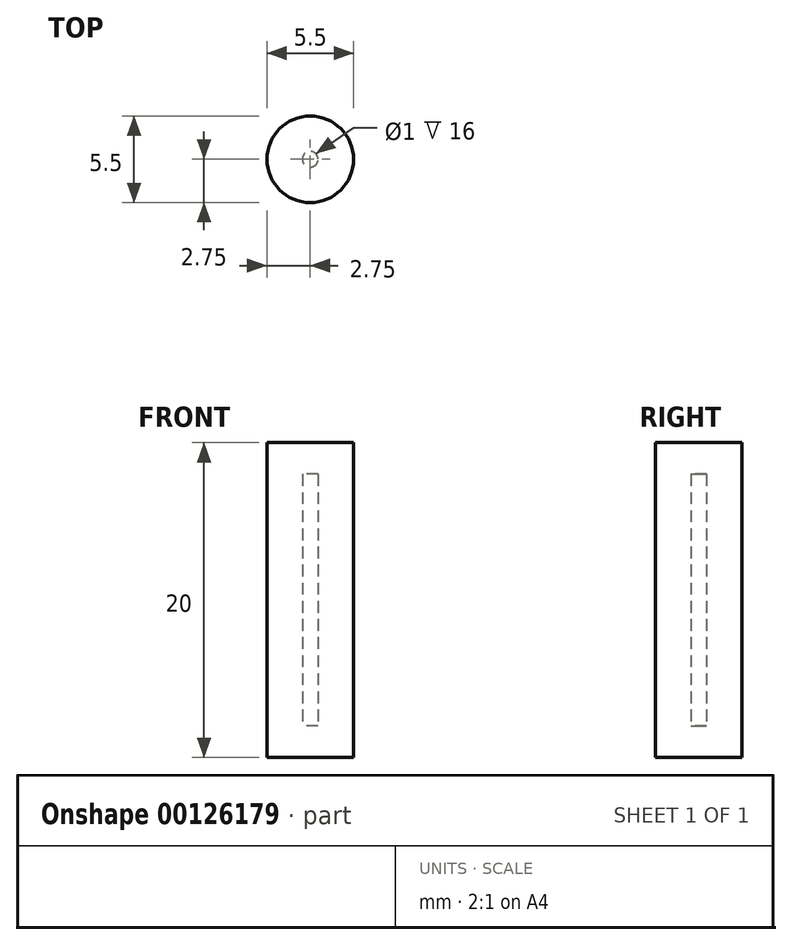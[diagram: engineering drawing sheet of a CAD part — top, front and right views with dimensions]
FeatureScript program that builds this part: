
annotation { "Feature Type Name" : "Feature", "Feature Type Description" : "" }
export const myFeature = defineFeature(function(context is Context, id is Id, definition is map)
    precondition{}
    {
        {
            var Q0;
            Q0=qCreatedBy(makeId("Top.planeOp"),FACE);
            var sketch = newSketch(context, id + "F0", { "sketchPlane" : qUnion([Q0])});
            skCircle(sketch, "E0", {"center": v(0, 0) * mm, "radius": 2.75 * mm});
            skSolve(sketch);
        }
        {
            var Q0;
            Q0 = qSketchRegion(id + "F0", true);
            extrude(context, id + "F1", {"entities" : qUnion([Q0]), "depth" : 2 * mm});
        }
        {
            var Q0;
            Q0=makeQuery(id+"F1.opExtrude","CAP_FACE",FACE,{"disambiguationData":[OSD([sQuery(id+"F0.wireOp",EDGE,"E0")])],"isStart":false});
            var sketch = newSketch(context, id + "F2", { "sketchPlane" : qUnion([Q0])});
            skCircle(sketch, "E1", {"center": v(0, 0) * mm, "radius": 2.75 * mm});
            skCircle(sketch, "E2", {"center": v(0, 0) * mm, "radius": 0.5 * mm});
            skSolve(sketch);
        }
        {
            var Q0;
            Q0 = qSketchRegion(id + "F2", true);
            extrude(context, id + "F3", {"entities" : qUnion([Q0]), "operationType" : NewBodyOperationType.ADD, "depth" : 16 * mm});
        }
        {
            var Q0;
            Q0=makeQuery(id+"F3.opExtrude","CAP_FACE",FACE,{"disambiguationData":[OSD([sQuery(id+"F2.wireOp",EDGE,"E1"),sQuery(id+"F2.wireOp",EDGE,"E2")])],"isStart":false});
            var sketch = newSketch(context, id + "F4", { "sketchPlane" : qUnion([Q0])});
            skCircle(sketch, "E3", {"center": v(0, 0) * mm, "radius": 2.75 * mm});
            skSolve(sketch);
        }
        {
            var Q0;
            Q0 = qSketchRegion(id + "F4", true);
            extrude(context, id + "F5", {"entities" : qUnion([Q0]), "operationType" : NewBodyOperationType.ADD, "depth" : 2 * mm});
        }
    });
